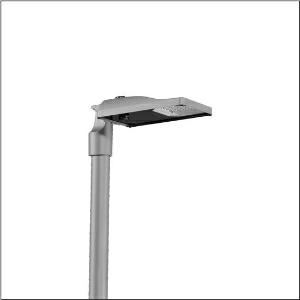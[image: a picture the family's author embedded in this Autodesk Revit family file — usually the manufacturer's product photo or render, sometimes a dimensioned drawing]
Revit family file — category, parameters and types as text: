
# Revit family: streetlight_sl_31_micro___st0_5a_5xh5b31t08ca_3c37
name_source: partatom
category: Lighting Fixtures
units: mm (PartAtom-declared; Revit-internal decimal feet)

## family parameters
Cut with Voids When Loaded = No
Host = Face
Light Source = No
Part Type = Normal
Room Calculation Point = No
Round Connector Dimension = Use Diameter
Shared = No

## types (1)
- --- (1 x LED, 1440 lm, 10.2 W, 3000K)
    Apparent Load = 10 VA
    CIE Flux Codes = 41 75 97 100 100
    Color Rendering = 70
    Color Temperature = 3000K
    Default Elevation = 1800 mm
    Description = Streetlight SL 31 micro, mast luminaire, primary light control with lens, of PMMA, primary optical cover: cover, of toughened safety glass, transparent, light distribution: ST0.5a, light emission: direct distribution, primary light characteristic: asymmetric, installation type: post-top, side-entry, LED, High Power LED, rated luminous flux: 1.440lm, luminous efficacy: 141lm/W, light colour: 730, colour temperature: 3000K, control: presetting dimming logarithmic, flexible luminous flux parameterisation, time-dependent luminous flux control, constant luminous flux control, power reduction, intelligent temperature release in ECG and LED module, overheat protection, with cable H07RN-F 2x 1.5mm², mains connection: 220..240V, AC, 50/60Hz, connection cable pre-assembled, cable length: 5,5m, start of lifetime: 10W, end of service life: 11W, reduction: 5W, luminaire housing, of diecast aluminium, powder-coated, Siteco® metallic grey (DB 702S), corrosivity category C5 high according to DIN EN ISO 12944, sealing non-destructively replaceable, multi-level sealing system, mast flange (76/60mm) included as standard, inclination: -15°..+20° (post-top) | -20°..+20° (side-entry), adjustable in 5° steps, no sealing on luminaire upper side, Smart Interface below and above, protection rating (complete): IP66, insulation class (complete): insulation class II (safety insulation), certification: CE, ENEC, ENEC+, VDE, UKCA, ZD4i, impact resistance: IK09, permissible operating ambient temperature for outdoor applications: -40..+50°C, standard-compliant lighting for roads and squares, packaging unit: 1 piece

Light Distribution: ST0.5a
    Height = 76 mm
    Lamp = 1 x LED
    Lamp Light Flux = 1440 lm
    Lamp Power = 10.2 W
    Lamp count = 1
    Length = 467 mm
    Luminous efficacy = 141 lm/W
    Manufacturer = Siteco
    ModVariant = No
    Model = 5XH5B31T08CA
    Number of Poles = 1
    OnlyDefault = Yes
    Power Factor = 1
    Product Name = Streetlight SL 31 micro | ST0.5a
    Product group = mast luminaire | pylon top
    ProductGroupID = 6100
    Protection Class = Protection class II
    Protection Degree = IP 66
    RLX_Detail_Level = 1
    RLX_Emergency_Light_Flux = 0 lm
    RLX_Emergency_Type = 0
    RLX_Emergency_Type_DB = No
    RlxData = <blob elided: 55537 chars, md5=98eb0280>
    Socket = socket
    Standby Power = 0 W
    System Light Flux = 1440 lm
    System Power = 10 W
    Type Comments = factory setting: luminous flux: 100 % | dim-lin: 254 | 386 mA
    Type Image = l_1300315.jpg
    URL = http://relux.com
    VarID = @adj_006251
    Voltage = 0 V
    Weight = 0.00 kg
    Width = 265 mm

## geometry (parser evidence)
native form markers: Blend x4, Sweep x11
no freeform markers — native parametric forms only
